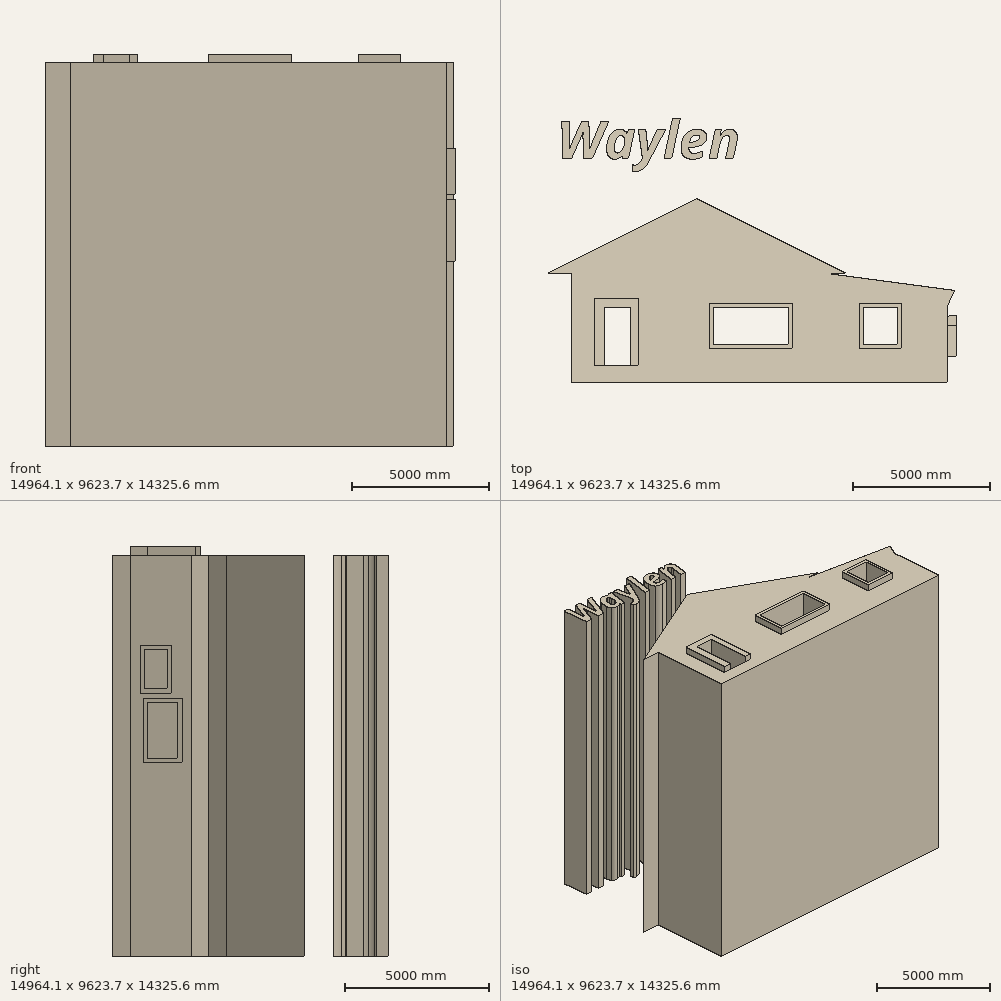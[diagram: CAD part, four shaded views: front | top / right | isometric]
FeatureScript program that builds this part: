
annotation { "Feature Type Name" : "Feature", "Feature Type Description" : "" }
export const myFeature = defineFeature(function(context is Context, id is Id, definition is map)
    precondition{}
    {
        {
            var Q0;
            Q0=qCreatedBy(makeId("Top.planeOp"),FACE);
            var sketch = newSketch(context, id + "F0", { "sketchPlane" : qUnion([Q0])});
            skLineSegment(sketch, "E0", {"start": v(0, 0) * mm, "end": v(4572, 0) * mm});
            skLineSegment(sketch, "E1", {"start": v(0, 0) * mm, "end": v(-4572, 0) * mm});
            skLineSegment(sketch, "E2", {"start": v(0, 0) * mm, "end": v(0, 2286) * mm});
            skLineSegment(sketch, "E3", {"start": v(0, 2286) * mm, "end": v(-4572, 0) * mm});
            skLineSegment(sketch, "E4", {"start": v(0, 2286) * mm, "end": v(4572, 0) * mm});
            skLineSegment(sketch, "E5", {"start": v(-4572, 0) * mm, "end": v(-5486.4, 0) * mm});
            skLineSegment(sketch, "E6", {"start": v(4572, 0) * mm, "end": v(5486.4, 0) * mm});
            skLineSegment(sketch, "E7", {"start": v(0, 2286) * mm, "end": v(0, 2743.2) * mm});
            skLineSegment(sketch, "E8", {"start": v(-5486.4, 0) * mm, "end": v(0, 2743.2) * mm});
            skLineSegment(sketch, "E9", {"start": v(5486.4, 0) * mm, "end": v(0, 2743.2) * mm});
            skLineSegment(sketch, "E10", {"start": v(-4572, 0) * mm, "end": v(-4572, -3352.8) * mm});
            skLineSegment(sketch, "E11", {"start": v(4572, 0) * mm, "end": v(4572, -3352.8) * mm});
            skLineSegment(sketch, "E12", {"start": v(-4572, -3352.8) * mm, "end": v(4572, -3352.8) * mm});
            skLineSegment(sketch, "E13", {"start": v(-4572, -3352.8) * mm, "end": v(-4572, -3962.4) * mm});
            skLineSegment(sketch, "E14", {"start": v(4572, -3352.8) * mm, "end": v(4572, -3962.4) * mm});
            skLineSegment(sketch, "E15", {"start": v(-4572, -3962.4) * mm, "end": v(4572, -3962.4) * mm});
            skLineSegment(sketch, "E16", {"start": v(4572, -3962.4) * mm, "end": v(9144, -3962.4) * mm});
            skLineSegment(sketch, "E17", {"start": v(4572, -3352.8) * mm, "end": v(9144, -3352.8) * mm});
            skLineSegment(sketch, "E18", {"start": v(9144, -3352.8) * mm, "end": v(9144, -3962.4) * mm});
            skLineSegment(sketch, "E19", {"start": v(-3352.8, -3352.8) * mm, "end": v(-3352.8, -1219.2) * mm});
            skLineSegment(sketch, "E20", {"start": v(-3352.8, -1219.2) * mm, "end": v(-2438.4, -1219.2) * mm});
            skLineSegment(sketch, "E21", {"start": v(-2438.4, -1219.2) * mm, "end": v(-2438.4, -3352.8) * mm});
            skLineSegment(sketch, "E22", {"start": v(4572, -1090.49) * mm, "end": v(4572, 0) * mm});
            skLineSegment(sketch, "E23", {"start": v(4572, -545.24) * mm, "end": v(4844.62, 0) * mm});
            skLineSegment(sketch, "E24", {"start": v(4844.62, 0) * mm, "end": v(9415.78, -609.6) * mm});
            skLineSegment(sketch, "E25", {"start": v(4572, -545.24) * mm, "end": v(9134.11, -1219.2) * mm});
            skLineSegment(sketch, "E26", {"start": v(9134.11, -1219.2) * mm, "end": v(9144, -3352.8) * mm});
            skLineSegment(sketch, "E27", {"start": v(9134.11, -1219.2) * mm, "end": v(9415.78, -609.6) * mm});
            skLineSegment(sketch, "E28", {"start": v(609.6, -2590.8) * mm, "end": v(3352.8, -2590.8) * mm});
            skLineSegment(sketch, "E29", {"start": v(609.6, -2590.8) * mm, "end": v(609.6, -1219.2) * mm});
            skLineSegment(sketch, "E30", {"start": v(3352.8, -2590.8) * mm, "end": v(3352.8, -1219.2) * mm});
            skLineSegment(sketch, "E31", {"start": v(609.6, -1219.2) * mm, "end": v(3352.8, -1219.2) * mm});
            skLineSegment(sketch, "E32", {"start": v(-2133.6, -3352.8) * mm, "end": v(-2133.6, -914.4) * mm});
            skLineSegment(sketch, "E33", {"start": v(-3724.72, -3352.8) * mm, "end": v(-3724.72, -914.4) * mm});
            skLineSegment(sketch, "E34", {"start": v(-3724.72, -914.4) * mm, "end": v(-2133.6, -914.4) * mm});
            skLineSegment(sketch, "E35", {"start": v(6096, -2590.8) * mm, "end": v(7315.2, -2590.8) * mm});
            skLineSegment(sketch, "E36", {"start": v(6096, -2590.8) * mm, "end": v(6096, -1219.2) * mm});
            skLineSegment(sketch, "E37", {"start": v(7315.2, -2590.8) * mm, "end": v(7315.2, -1219.2) * mm});
            skLineSegment(sketch, "E38", {"start": v(6096, -1219.2) * mm, "end": v(7315.2, -1219.2) * mm});
            skLineSegment(sketch, "E39.0", {"start": v(604.6, -1214.2) * mm, "end": v(3357.8, -1214.2) * mm});
            skLineSegment(sketch, "E39.1", {"start": v(604.6, -2595.8) * mm, "end": v(604.6, -1214.2) * mm});
            skLineSegment(sketch, "E39.2", {"start": v(604.6, -2595.8) * mm, "end": v(3357.8, -2595.8) * mm});
            skLineSegment(sketch, "E39.3", {"start": v(3357.8, -2595.8) * mm, "end": v(3357.8, -1214.2) * mm});
            skLineSegment(sketch, "E40.0", {"start": v(457.2, -1066.8) * mm, "end": v(3505.2, -1066.8) * mm});
            skLineSegment(sketch, "E40.1", {"start": v(457.2, -2743.2) * mm, "end": v(457.2, -1066.8) * mm});
            skLineSegment(sketch, "E40.2", {"start": v(457.2, -2743.2) * mm, "end": v(3505.2, -2743.2) * mm});
            skLineSegment(sketch, "E40.3", {"start": v(3505.2, -2743.2) * mm, "end": v(3505.2, -1066.8) * mm});
            skLineSegment(sketch, "E41.0", {"start": v(5943.6, -2743.2) * mm, "end": v(5943.6, -1066.8) * mm});
            skLineSegment(sketch, "E41.1", {"start": v(5943.6, -2743.2) * mm, "end": v(7467.6, -2743.2) * mm});
            skLineSegment(sketch, "E41.2", {"start": v(7467.6, -2743.2) * mm, "end": v(7467.6, -1066.8) * mm});
            skLineSegment(sketch, "E41.3", {"start": v(5943.6, -1066.8) * mm, "end": v(7467.6, -1066.8) * mm});
            skText(sketch, "E42", { "text": "Waylen\n", "fontName": "OpenSans-BoldItalic.ttf"});
            const initialGuessF0  = {"E42": [-5.10244, 4.19631, 1, 0, 1.38819]};
            skSetInitialGuess(sketch, initialGuessF0);
            skSolve(sketch);
        }
        {
            var Q0;
            {var subQ3=sQuery(id+"F0.wireOp",EDGE,"E4");Q0=makeQuery(id+"F0.imprint","IMPRINT",FACE,{"disambiguationData":[TD([[makeQuery(id+"F0.imprint","IMPRINT",EDGE,{"derivedFrom":subQ3}),1.0]])]});}
            var Q1;
            Q1=makeQuery(id+"F0.imprint","IMPRINT",FACE,{"disambiguationData":[TD([[makeQuery(id+"F0.imprint","IMPRINT",EDGE,{"derivedFrom":sQuery(id+"F0.wireOp",EDGE,"E3")}),-1.0]])]});
            extrude(context, id + "F1", {"entities" : qUnion([Q0, Q1]), "depth" : 914.4 * mm, "offsetDistance" : 30.48 * mm});
        }
        {
            var Q0;
            Q0=makeQuery(id+"F0.imprint","IMPRINT",FACE,{"disambiguationData":[TD([[makeQuery(id+"F0.imprint","IMPRINT",EDGE,{"derivedFrom":sQuery(id+"F0.wireOp",EDGE,"E1")}),-1.0]])]});
            var Q1;
            Q1=makeQuery(id+"F0.imprint","IMPRINT",FACE,{"disambiguationData":[TD([[makeQuery(id+"F0.imprint","IMPRINT",EDGE,{"derivedFrom":sQuery(id+"F0.wireOp",EDGE,"E0")}),1.0]])]});
            extrude(context, id + "F2", {"entities" : qUnion([Q0, Q1]), "operationType" : NewBodyOperationType.ADD, "depth" : -12192 * mm, "offsetDistance" : 30.48 * mm});
        }
        {
            var Q0;
            Q0 = qSketchRegion(id + "F0", true);
            extrude(context, id + "F3", {"entities" : qUnion([Q0]), "operationType" : NewBodyOperationType.ADD, "depth" : 914.4 * mm, "offsetDistance" : 30.48 * mm, "hasSecondDirection" : true, "secondDirectionOppositeDirection" : true, "secondDirectionDepth" : 13106.4 * mm});
        }
        {
            var Q0;
            Q0=makeQuery(id+"F0.imprint","IMPRINT",FACE,{"disambiguationData":[TD([[makeQuery(id+"F0.imprint","IMPRINT",EDGE,{"derivedFrom":sQuery(id+"F0.wireOp",EDGE,"E39.0")}),1.0]])]});
            var Q1;
            Q1=makeQuery(id+"F0.imprint","IMPRINT",FACE,{"disambiguationData":[TD([[makeQuery(id+"F0.imprint","IMPRINT",EDGE,{"derivedFrom":sQuery(id+"F0.wireOp",EDGE,"E35")}),-1.0]])]});
            var Q2;
            {var subQ0=sQuery(id+"F0.wireOp",EDGE,"E19");Q2=makeQuery(id+"F0.imprint","IMPRINT",FACE,{"disambiguationData":[TD([[makeQuery(id+"F0.imprint","IMPRINT",EDGE,{"derivedFrom":subQ0}),1.0]])]});}
            extrude(context, id + "F4", {"entities" : qUnion([Q0, Q1, Q2]), "operationType" : NewBodyOperationType.ADD, "depth" : 1219.2 * mm, "offsetDistance" : 30.48 * mm});
        }
        {
            var Q0;
            Q0=makeQuery(id+"F0.imprint","IMPRINT",FACE,{"disambiguationData":[TD([[makeQuery(id+"F0.imprint","IMPRINT",EDGE,{"derivedFrom":sQuery(id+"F0.wireOp",EDGE,"E0")}),1.0]])]});
            var Q1;
            Q1=makeQuery(id+"F0.imprint","IMPRINT",FACE,{"disambiguationData":[TD([[makeQuery(id+"F0.imprint","IMPRINT",EDGE,{"derivedFrom":sQuery(id+"F0.wireOp",EDGE,"E1")}),-1.0]])]});
            extrude(context, id + "F5", {"entities" : qUnion([Q0, Q1]), "operationType" : NewBodyOperationType.ADD, "depth" : 914.4 * mm, "offsetDistance" : 30.48 * mm});
        }
        {
            var Q0;
            {var subQ0=sQuery(id+"F0.wireOp",EDGE,"E19");Q0=makeQuery(id+"F0.imprint","IMPRINT",FACE,{"disambiguationData":[TD([[makeQuery(id+"F0.imprint","IMPRINT",EDGE,{"derivedFrom":subQ0}),1.0]])]});}
            var Q1;
            Q1=makeQuery(id+"F0.imprint","IMPRINT",FACE,{"disambiguationData":[TD([[makeQuery(id+"F0.imprint","IMPRINT",EDGE,{"derivedFrom":sQuery(id+"F0.wireOp",EDGE,"E39.0")}),1.0]])]});
            var Q2;
            Q2=makeQuery(id+"F0.imprint","IMPRINT",FACE,{"disambiguationData":[TD([[makeQuery(id+"F0.imprint","IMPRINT",EDGE,{"derivedFrom":sQuery(id+"F0.wireOp",EDGE,"E35")}),-1.0]])]});
            extrude(context, id + "F6", {"entities" : qUnion([Q0, Q1, Q2]), "operationType" : NewBodyOperationType.ADD, "depth" : 914.4 * mm, "offsetDistance" : 30.48 * mm, "hasSecondDirection" : true, "secondDirectionOppositeDirection" : true, "secondDirectionDepth" : 0 * mm});
        }
        {
            var Q0;
            Q0=makeQuery(id+"F3.opExtrude","SWEPT_FACE",FACE,{"disambiguationData":[OSD([sQuery(id+"F0.wireOp",EDGE,"E26")])]});
            var sketch = newSketch(context, id + "F7", { "sketchPlane" : qUnion([Q0])});
            skLineSegment(sketch, "E43.bottom", {"start": v(-3049.84, -2225.57) * mm, "end": v(-1939.57, -2225.57) * mm});
            skLineSegment(sketch, "E43.top", {"start": v(-3049.84, -3901.18) * mm, "end": v(-1939.57, -3901.18) * mm});
            skLineSegment(sketch, "E43.left", {"start": v(-3049.84, -2225.57) * mm, "end": v(-3049.84, -3901.18) * mm});
            skLineSegment(sketch, "E43.right", {"start": v(-1939.57, -2225.57) * mm, "end": v(-1939.57, -3901.18) * mm});
            skLineSegment(sketch, "E44.0", {"start": v(-2897.44, -2377.97) * mm, "end": v(-2091.97, -2377.97) * mm});
            skLineSegment(sketch, "E44.1", {"start": v(-2897.44, -2377.97) * mm, "end": v(-2897.44, -3748.78) * mm});
            skLineSegment(sketch, "E44.2", {"start": v(-2897.44, -3748.78) * mm, "end": v(-2091.97, -3748.78) * mm});
            skLineSegment(sketch, "E44.3", {"start": v(-2091.97, -2377.97) * mm, "end": v(-2091.97, -3748.78) * mm});
            skLineSegment(sketch, "E45.bottom", {"start": v(-1736.47, -4228.17) * mm, "end": v(-2795.58, -4228.17) * mm});
            skLineSegment(sketch, "E45.top", {"start": v(-1736.47, -6175.42) * mm, "end": v(-2795.58, -6175.42) * mm});
            skLineSegment(sketch, "E45.left", {"start": v(-1736.47, -4228.17) * mm, "end": v(-1736.47, -6175.42) * mm});
            skLineSegment(sketch, "E45.right", {"start": v(-2795.58, -4228.17) * mm, "end": v(-2795.58, -6175.42) * mm});
            skLineSegment(sketch, "E46.0", {"start": v(-1584.07, -4075.77) * mm, "end": v(-2947.98, -4075.77) * mm});
            skLineSegment(sketch, "E46.1", {"start": v(-1584.07, -4075.77) * mm, "end": v(-1584.07, -6327.82) * mm});
            skLineSegment(sketch, "E46.2", {"start": v(-1584.07, -6327.82) * mm, "end": v(-2947.98, -6327.82) * mm});
            skLineSegment(sketch, "E46.3", {"start": v(-2947.98, -4075.77) * mm, "end": v(-2947.98, -6327.82) * mm});
            skSolve(sketch);
        }
        {
            var Q0;
            Q0 = qSketchRegion(id + "F7", true);
            extrude(context, id + "F8", {"entities" : qUnion([Q0]), "operationType" : NewBodyOperationType.ADD, "depth" : 30.48 * mm, "offsetDistance" : 30.48 * mm});
        }
        {
            var Q0;
            Q0=makeQuery(id+"F8.opExtrude","CAP_FACE",FACE,{"disambiguationData":[OSD([sQuery(id+"F7.wireOp",EDGE,"E45.bottom"),sQuery(id+"F7.wireOp",EDGE,"E45.top"),sQuery(id+"F7.wireOp",EDGE,"E45.left"),sQuery(id+"F7.wireOp",EDGE,"E45.right"),sQuery(id+"F7.wireOp",EDGE,"E46.0"),sQuery(id+"F7.wireOp",EDGE,"E46.1"),sQuery(id+"F7.wireOp",EDGE,"E46.2"),sQuery(id+"F7.wireOp",EDGE,"E46.3")])],"isStart":false});
            var sketch = newSketch(context, id + "F9", { "sketchPlane" : qUnion([Q0])});
            skSolve(sketch);
        }
        {
            var Q0;
            Q0=makeQuery(id+"F9.imprint","IMPRINT",FACE,{"disambiguationData":[TD([[makeQuery(id+"F9.imprint","IMPRINT",EDGE,{"derivedFrom":makeQuery(id+"F8.opExtrude","CAP_EDGE",EDGE,{"disambiguationData":[OSD([sQuery(id+"F7.wireOp",EDGE,"E45.bottom")])],"isStart":false})}),-1.0]])]});
            var Q1;
            Q1=makeQuery(id+"F8.opExtrude","CAP_FACE",FACE,{"disambiguationData":[OSD([sQuery(id+"F7.wireOp",EDGE,"E43.bottom"),sQuery(id+"F7.wireOp",EDGE,"E43.top"),sQuery(id+"F7.wireOp",EDGE,"E43.left"),sQuery(id+"F7.wireOp",EDGE,"E43.right"),sQuery(id+"F7.wireOp",EDGE,"E44.0"),sQuery(id+"F7.wireOp",EDGE,"E44.1"),sQuery(id+"F7.wireOp",EDGE,"E44.2"),sQuery(id+"F7.wireOp",EDGE,"E44.3")])],"isStart":false});
            extrude(context, id + "F10", {"entities" : qUnion([Q0, Q1]), "operationType" : NewBodyOperationType.ADD, "depth" : 304.8 * mm, "offsetDistance" : 30.48 * mm});
        }
    });
